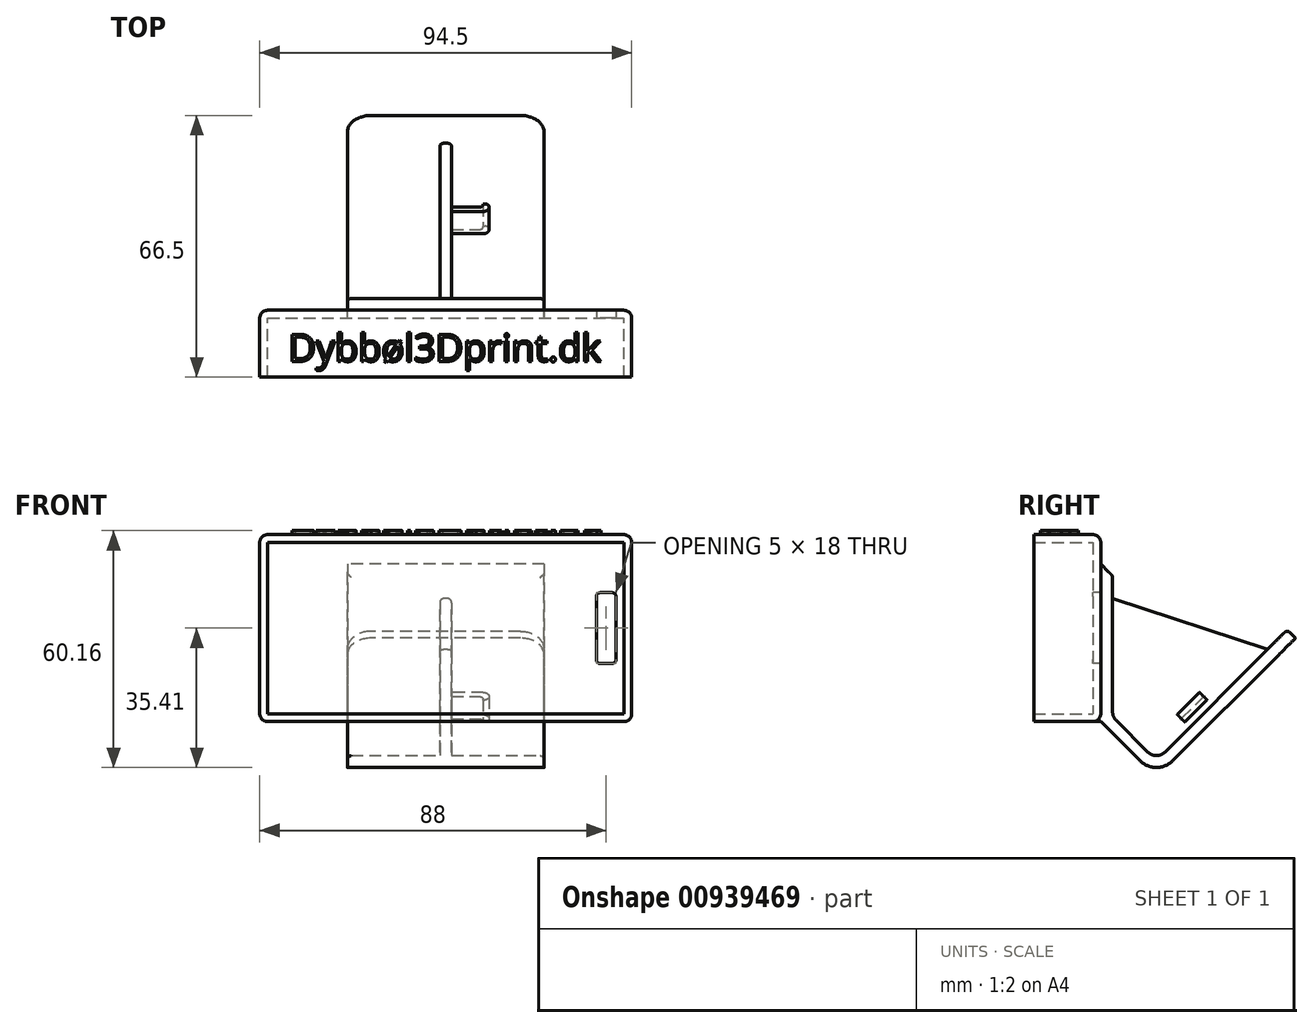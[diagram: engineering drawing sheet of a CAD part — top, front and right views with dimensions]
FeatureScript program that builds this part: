
annotation { "Feature Type Name" : "Feature", "Feature Type Description" : "" }
export const myFeature = defineFeature(function(context is Context, id is Id, definition is map)
    precondition{}
    {
        {
            var Q0;
            Q0=qCreatedBy(makeId("Front.planeOp"),FACE);
            var sketch = newSketch(context, id + "F0", { "sketchPlane" : qUnion([Q0])});
            skLineSegment(sketch, "E0.bottom", {"start": v(-47.25, 23.75) * mm, "end": v(47.25, 23.75) * mm});
            skLineSegment(sketch, "E0.top", {"start": v(-47.25, -23.75) * mm, "end": v(47.25, -23.75) * mm});
            skLineSegment(sketch, "E0.left", {"start": v(-47.25, 23.75) * mm, "end": v(-47.25, -23.75) * mm});
            skLineSegment(sketch, "E0.right", {"start": v(47.25, 23.75) * mm, "end": v(47.25, -23.75) * mm});
            skSolve(sketch);
        }
        {
            var Q0;
            Q0 = qSketchRegion(id + "F0", true);
            extrude(context, id + "F1", {"entities" : qUnion([Q0]), "depth" : 17 * mm, "offsetDistance" : 25 * mm});
        }
        {
            var Q0;
            Q0=makeQuery(id+"F1.opExtrude","CAP_FACE",FACE,{"disambiguationData":[OSD([sQuery(id+"F0.wireOp",EDGE,"E0.bottom"),sQuery(id+"F0.wireOp",EDGE,"E0.top"),sQuery(id+"F0.wireOp",EDGE,"E0.left"),sQuery(id+"F0.wireOp",EDGE,"E0.right")])],"isStart":false});
            shell(context, id + "F2", {"entities" : qUnion([Q0]), "thickness" : 2 * mm});
        }
        {
            var Q0;
            Q0=qCreatedBy(makeId("Right.planeOp"),FACE);
            var sketch = newSketch(context, id + "F3", { "sketchPlane" : qUnion([Q0])});
            skLineSegment(sketch, "E1.0", {"start": v(-17, -23.75) * mm, "end": v(0, -23.75) * mm, "construction": true});
            skLineSegment(sketch, "E2", {"start": v(0, -23.75) * mm, "end": v(14.14, -37.9) * mm});
            skLineSegment(sketch, "E3", {"start": v(14.14, -37.9) * mm, "end": v(49.5, -2.54) * mm});
            skLineSegment(sketch, "E4", {"start": v(49.5, -2.54) * mm, "end": v(47.38, -0.42) * mm});
            skLineSegment(sketch, "E5", {"start": v(47.38, -0.42) * mm, "end": v(14.14, -33.65) * mm});
            skLineSegment(sketch, "E6", {"start": v(14.14, -33.65) * mm, "end": v(3, -22.5) * mm});
            skLineSegment(sketch, "E7", {"start": v(3, -22.5) * mm, "end": v(3, 13.25) * mm});
            skLineSegment(sketch, "E8", {"start": v(0, 0) * mm, "end": v(0, -23.75) * mm});
            skLineSegment(sketch, "E9", {"start": v(0, 0) * mm, "end": v(0, 16.25) * mm});
            skLineSegment(sketch, "E10", {"start": v(0, 16.25) * mm, "end": v(3, 13.25) * mm});
            skSolve(sketch);
        }
        {
            var Q0;
            Q0 = qSketchRegion(id + "F3", true);
            extrude(context, id + "F4", {"entities" : qUnion([Q0]), "operationType" : NewBodyOperationType.ADD, "endBound" : BoundingType.SYMMETRIC, "depth" : 50 * mm, "offsetDistance" : 25 * mm});
        }
        {
            var Q0;
            Q0=qCreatedBy(makeId("Right.planeOp"),FACE);
            var sketch = newSketch(context, id + "F5", { "sketchPlane" : qUnion([Q0])});
            skLineSegment(sketch, "E11.0", {"start": v(14.14, -33.65) * mm, "end": v(3, -22.5) * mm});
            skLineSegment(sketch, "E12.0", {"start": v(3, -22.5) * mm, "end": v(3, 7.5) * mm});
            skLineSegment(sketch, "E13.0", {"start": v(42.43, -5.37) * mm, "end": v(14.14, -33.65) * mm});
            skLineSegment(sketch, "E14", {"start": v(3, 7.5) * mm, "end": v(42.43, -5.37) * mm});
            skPoint(sketch, "E15.orphan", {"position": v(47.38, -0.42) * mm});
            skPoint(sketch, "E16.orphan", {"position": v(3, 13.25) * mm});
            skSolve(sketch);
        }
        {
            var Q0;
            Q0 = qSketchRegion(id + "F5", true);
            extrude(context, id + "F6", {"entities" : qUnion([Q0]), "operationType" : NewBodyOperationType.ADD, "endBound" : BoundingType.SYMMETRIC, "depth" : 3 * mm, "offsetDistance" : 25 * mm});
        }
        {
            var Q0;
            {var subQ0=sQuery(id+"F3.wireOp",EDGE,"E6");var subQ1=sQuery(id+"F3.wireOp",EDGE,"E5");Q0=makeQuery(id+"F6.boolean.opBoolean","SPLIT",EDGE,{"disambiguationData":[TD([makeQuery(id+"F6.opExtrude","CAP_FACE",FACE,{"disambiguationData":[OSD([sQuery(id+"F5.wireOp",EDGE,"E11.0"),sQuery(id+"F5.wireOp",EDGE,"E12.0"),sQuery(id+"F5.wireOp",EDGE,"E13.0"),sQuery(id+"F5.wireOp",EDGE,"E14")])],"isStart":false})])],"derivedFrom":makeQuery(id+"F4.opExtrude","SWEPT_EDGE",EDGE,{"disambiguationData":[OSD([subQ1,subQ0])]})});}
            var Q1;
            {var subQ0=sQuery(id+"F3.wireOp",EDGE,"E7");var subQ1=sQuery(id+"F3.wireOp",EDGE,"E6");Q1=makeQuery(id+"F6.boolean.opBoolean","SPLIT",EDGE,{"disambiguationData":[TD([makeQuery(id+"F6.opExtrude","CAP_FACE",FACE,{"disambiguationData":[OSD([sQuery(id+"F5.wireOp",EDGE,"E11.0"),sQuery(id+"F5.wireOp",EDGE,"E12.0"),sQuery(id+"F5.wireOp",EDGE,"E13.0"),sQuery(id+"F5.wireOp",EDGE,"E14")])],"isStart":false})])],"derivedFrom":makeQuery(id+"F4.opExtrude","SWEPT_EDGE",EDGE,{"disambiguationData":[OSD([subQ1,subQ0])]})});}
            var Q2;
            {var subQ0=sQuery(id+"F3.wireOp",EDGE,"E6");var subQ1=sQuery(id+"F3.wireOp",EDGE,"E5");Q2=makeQuery(id+"F6.boolean.opBoolean","SPLIT",EDGE,{"disambiguationData":[TD([makeQuery(id+"F6.opExtrude","CAP_FACE",FACE,{"disambiguationData":[OSD([sQuery(id+"F5.wireOp",EDGE,"E11.0"),sQuery(id+"F5.wireOp",EDGE,"E12.0"),sQuery(id+"F5.wireOp",EDGE,"E13.0"),sQuery(id+"F5.wireOp",EDGE,"E14")])],"isStart":true})])],"derivedFrom":makeQuery(id+"F4.opExtrude","SWEPT_EDGE",EDGE,{"disambiguationData":[OSD([subQ1,subQ0])]})});}
            var Q3;
            {var subQ0=sQuery(id+"F3.wireOp",EDGE,"E7");var subQ1=sQuery(id+"F3.wireOp",EDGE,"E6");Q3=makeQuery(id+"F6.boolean.opBoolean","SPLIT",EDGE,{"disambiguationData":[TD([makeQuery(id+"F6.opExtrude","CAP_FACE",FACE,{"disambiguationData":[OSD([sQuery(id+"F5.wireOp",EDGE,"E11.0"),sQuery(id+"F5.wireOp",EDGE,"E12.0"),sQuery(id+"F5.wireOp",EDGE,"E13.0"),sQuery(id+"F5.wireOp",EDGE,"E14")])],"isStart":true})])],"derivedFrom":makeQuery(id+"F4.opExtrude","SWEPT_EDGE",EDGE,{"disambiguationData":[OSD([subQ1,subQ0])]})});}
            fillet(context, id + "F7", {"entities" : qUnion([Q0, Q1, Q2, Q3]), "tangentPropagation" : true, "radius" : 3 * mm, "defaultsChanged" : false, "vertexSettings" : [], "allowEdgeOverflow" : false});
        }
        {
            var Q0;
            Q0=makeQuery(id+"F4.opExtrude","SWEPT_EDGE",EDGE,{"disambiguationData":[OSD([sQuery(id+"F3.wireOp",EDGE,"E2"),sQuery(id+"F3.wireOp",EDGE,"E3")])]});
            var Q1;
            Q1=makeQuery(id+"F4.opExtrude","CAP_EDGE",EDGE,{"disambiguationData":[OSD([sQuery(id+"F3.wireOp",EDGE,"E4")])],"isStart":false});
            var Q2;
            Q2=makeQuery(id+"F4.opExtrude","CAP_EDGE",EDGE,{"disambiguationData":[OSD([sQuery(id+"F3.wireOp",EDGE,"E4")])],"isStart":true});
            fillet(context, id + "F8", {"entities" : qUnion([Q0, Q1, Q2]), "tangentPropagation" : true, "radius" : 6 * mm, "defaultsChanged" : false, "vertexSettings" : [], "allowEdgeOverflow" : false});
        }
        {
            var Q0;
            Q0=makeQuery(id+"F1.opExtrude","SWEPT_EDGE",EDGE,{"disambiguationData":[OSD([sQuery(id+"F0.wireOp",EDGE,"E0.bottom"),sQuery(id+"F0.wireOp",EDGE,"E0.left")])]});
            var Q1;
            Q1=makeQuery(id+"F1.opExtrude","SWEPT_EDGE",EDGE,{"disambiguationData":[OSD([sQuery(id+"F0.wireOp",EDGE,"E0.top"),sQuery(id+"F0.wireOp",EDGE,"E0.left")])]});
            var Q2;
            Q2=makeQuery(id+"F1.opExtrude","SWEPT_EDGE",EDGE,{"disambiguationData":[OSD([sQuery(id+"F0.wireOp",EDGE,"E0.top"),sQuery(id+"F0.wireOp",EDGE,"E0.right")])]});
            var Q3;
            Q3=makeQuery(id+"F1.opExtrude","SWEPT_EDGE",EDGE,{"disambiguationData":[OSD([sQuery(id+"F0.wireOp",EDGE,"E0.bottom"),sQuery(id+"F0.wireOp",EDGE,"E0.right")])]});
            fillet(context, id + "F9", {"entities" : qUnion([Q0, Q1, Q2, Q3]), "tangentPropagation" : true, "radius" : 2 * mm, "defaultsChanged" : false, "vertexSettings" : [], "allowEdgeOverflow" : false});
        }
        {
            var Q0;
            Q0=makeQuery(id+"F1.opExtrude","CAP_EDGE",EDGE,{"disambiguationData":[OSD([sQuery(id+"F0.wireOp",EDGE,"E0.bottom")])],"isStart":true});
            fillet(context, id + "F10", {"entities" : qUnion([Q0]), "tangentPropagation" : true, "radius" : 2 * mm, "defaultsChanged" : false, "vertexSettings" : [], "allowEdgeOverflow" : false});
        }
        {
            var Q0;
            Q0=makeQuery(id+"F6.opExtrude","CAP_EDGE",EDGE,{"disambiguationData":[OSD([sQuery(id+"F5.wireOp",EDGE,"E14")])],"isStart":false});
            var Q1;
            Q1=makeQuery(id+"F6.opExtrude","CAP_EDGE",EDGE,{"disambiguationData":[OSD([sQuery(id+"F5.wireOp",EDGE,"E14")])],"isStart":true});
            var Q2;
            Q2=makeQuery(id+"F4.opExtrude","CAP_EDGE",EDGE,{"disambiguationData":[OSD([sQuery(id+"F3.wireOp",EDGE,"E5")])],"isStart":false});
            var Q3;
            Q3=makeQuery(id+"F4.opExtrude","SWEPT_EDGE",EDGE,{"disambiguationData":[OSD([sQuery(id+"F3.wireOp",EDGE,"E7"),sQuery(id+"F3.wireOp",EDGE,"E10")])]});
            fillet(context, id + "F11", {"entities" : qUnion([Q0, Q1, Q2, Q3]), "tangentPropagation" : true, "radius" : 1 * mm, "defaultsChanged" : false, "vertexSettings" : [], "allowEdgeOverflow" : false});
        }
        {
            var Q0;
            Q0=makeQuery(id+"F2.opShell","OFFSET_FACE",FACE,{"disambiguationData":[OSD([sQuery(id+"F0.wireOp",EDGE,"E0.bottom"),sQuery(id+"F0.wireOp",EDGE,"E0.top"),sQuery(id+"F0.wireOp",EDGE,"E0.left"),sQuery(id+"F0.wireOp",EDGE,"E0.right")])]});
            var sketch = newSketch(context, id + "F12", { "sketchPlane" : qUnion([Q0])});
            skLineSegment(sketch, "E17.bottom", {"start": v(43.25, 9) * mm, "end": v(38.25, 9) * mm});
            skLineSegment(sketch, "E17.top", {"start": v(43.25, -9) * mm, "end": v(38.25, -9) * mm});
            skLineSegment(sketch, "E17.left", {"start": v(43.25, 9) * mm, "end": v(43.25, -9) * mm});
            skLineSegment(sketch, "E17.right", {"start": v(38.25, 9) * mm, "end": v(38.25, -9) * mm});
            skSolve(sketch);
        }
        {
            var Q0;
            Q0 = qSketchRegion(id + "F12", true);
            extrude(context, id + "F13", {"entities" : qUnion([Q0]), "operationType" : NewBodyOperationType.REMOVE, "endBound" : BoundingType.THROUGH_ALL, "oppositeDirection" : true, "depth" : 25 * mm, "offsetDistance" : 25 * mm});
        }
        {
            var Q0;
            Q0=makeQuery(id+"F13.boolean.opBoolean","COPY",EDGE,{"derivedFrom":makeQuery(id+"F13.opExtrude","SWEPT_EDGE",EDGE,{"disambiguationData":[OSD([sQuery(id+"F12.wireOp",EDGE,"E17.top"),sQuery(id+"F12.wireOp",EDGE,"E17.left")])]})});
            var Q1;
            Q1=makeQuery(id+"F13.boolean.opBoolean","COPY",EDGE,{"derivedFrom":makeQuery(id+"F13.opExtrude","SWEPT_EDGE",EDGE,{"disambiguationData":[OSD([sQuery(id+"F12.wireOp",EDGE,"E17.top"),sQuery(id+"F12.wireOp",EDGE,"E17.right")])]})});
            var Q2;
            Q2=makeQuery(id+"F13.boolean.opBoolean","COPY",EDGE,{"derivedFrom":makeQuery(id+"F13.opExtrude","SWEPT_EDGE",EDGE,{"disambiguationData":[OSD([sQuery(id+"F12.wireOp",EDGE,"E17.bottom"),sQuery(id+"F12.wireOp",EDGE,"E17.left")])]})});
            var Q3;
            Q3=makeQuery(id+"F13.boolean.opBoolean","COPY",EDGE,{"derivedFrom":makeQuery(id+"F13.opExtrude","SWEPT_EDGE",EDGE,{"disambiguationData":[OSD([sQuery(id+"F12.wireOp",EDGE,"E17.bottom"),sQuery(id+"F12.wireOp",EDGE,"E17.right")])]})});
            fillet(context, id + "F14", {"entities" : qUnion([Q0, Q1, Q2, Q3]), "tangentPropagation" : true, "radius" : 1 * mm, "defaultsChanged" : false, "vertexSettings" : [], "allowEdgeOverflow" : false});
        }
        {
            var Q0;
            Q0=makeQuery(id+"F4.opExtrude","SWEPT_FACE",FACE,{"disambiguationData":[OSD([sQuery(id+"F3.wireOp",EDGE,"E4")])]});
            cPlane(context, id + "F15", {"entities" : qUnion([Q0]), "cplaneType" : CPlaneType.OFFSET, "offset" : 35 * mm, "oppositeDirection" : true, "width" : 150 * mm, "height" : 150 * mm});
        }
        {
            var Q0;
            Q0=qCreatedBy(id+"F15.planeOp",FACE);
            var sketch = newSketch(context, id + "F16", { "sketchPlane" : qUnion([Q0])});
            skLineSegment(sketch, "E18.0", {"start": v(-1.5, -33.8) * mm, "end": v(-1.5, 2.43) * mm, "construction": true});
            skLineSegment(sketch, "E19.0.0", {"start": v(-19, -33.8) * mm, "end": v(-19, -34.8) * mm, "construction": true});
            skLineSegment(sketch, "E19.0.1", {"start": v(19, -34.8) * mm, "end": v(-19, -34.8) * mm, "construction": true});
            skLineSegment(sketch, "E19.0.2", {"start": v(19, -34.8) * mm, "end": v(19, -33.8) * mm, "construction": true});
            skLineSegment(sketch, "E19.0.3", {"start": v(19, -33.8) * mm, "end": v(-19, -33.8) * mm, "construction": true});
            skLineSegment(sketch, "E20", {"start": v(-1.5, -30.8) * mm, "end": v(-9.5, -30.8) * mm});
            skLineSegment(sketch, "E21", {"start": v(-9.5, -32) * mm, "end": v(-9.5, -30.8) * mm});
            skLineSegment(sketch, "E22", {"start": v(-9.5, -32) * mm, "end": v(-11, -32) * mm});
            skLineSegment(sketch, "E23", {"start": v(-11, -29.3) * mm, "end": v(-11, -32) * mm});
            skLineSegment(sketch, "E24", {"start": v(-11, -29.3) * mm, "end": v(-1.5, -29.3) * mm});
            skLineSegment(sketch, "E25", {"start": v(-1.5, -30.8) * mm, "end": v(-1.5, -29.3) * mm});
            skSolve(sketch);
        }
        {
            var Q0;
            Q0 = qSketchRegion(id + "F16", true);
            extrude(context, id + "F17", {"entities" : qUnion([Q0]), "operationType" : NewBodyOperationType.ADD, "depth" : 8 * mm, "offsetDistance" : 25 * mm});
        }
        {
            var Q0;
            Q0=makeQuery(id+"F17.opExtrude","SWEPT_EDGE",EDGE,{"disambiguationData":[OSD([sQuery(id+"F16.wireOp",EDGE,"E20"),sQuery(id+"F16.wireOp",EDGE,"E25")])]});
            var Q1;
            Q1=makeQuery(id+"F17.opExtrude","SWEPT_EDGE",EDGE,{"disambiguationData":[OSD([sQuery(id+"F16.wireOp",EDGE,"E24"),sQuery(id+"F16.wireOp",EDGE,"E25")])]});
            var Q2;
            Q2=makeQuery(id+"F17.opExtrude","SWEPT_EDGE",EDGE,{"disambiguationData":[OSD([sQuery(id+"F16.wireOp",EDGE,"E20"),sQuery(id+"F16.wireOp",EDGE,"E21")])]});
            var Q3;
            Q3=makeQuery(id+"F17.opExtrude","SWEPT_EDGE",EDGE,{"disambiguationData":[OSD([sQuery(id+"F16.wireOp",EDGE,"E22"),sQuery(id+"F16.wireOp",EDGE,"E23")])]});
            fillet(context, id + "F18", {"entities" : qUnion([Q0, Q1, Q2, Q3]), "tangentPropagation" : true, "radius" : 1 * mm, "defaultsChanged" : false, "vertexSettings" : [], "allowEdgeOverflow" : false});
        }
        {
            var Q0;
            Q0=makeQuery(id+"F17.opExtrude","SWEPT_EDGE",EDGE,{"disambiguationData":[OSD([sQuery(id+"F16.wireOp",EDGE,"E23"),sQuery(id+"F16.wireOp",EDGE,"E24")])]});
            fillet(context, id + "F19", {"entities" : qUnion([Q0]), "tangentPropagation" : true, "radius" : 1.5 * mm, "defaultsChanged" : true, "vertexSettings" : [], "allowEdgeOverflow" : false});
        }
        {
            var Q0;
            Q0=makeQuery(id+"F1.opExtrude","SWEPT_FACE",FACE,{"disambiguationData":[OSD([sQuery(id+"F0.wireOp",EDGE,"E0.bottom")])]});
            var sketch = newSketch(context, id + "F20", { "sketchPlane" : qUnion([Q0])});
            skText(sketch, "E26", { "text": "Dybbøl3Dprint.dk", "fontName": "OpenSans-Regular.ttf"});
            const initialGuessF20  = {"E26": [-0.04, -0.013, 1, 0, 0.00693]};
            skSetInitialGuess(sketch, initialGuessF20);
            skSolve(sketch);
        }
        {
            var Q0;
            Q0 = qSketchRegion(id + "F20", true);
            extrude(context, id + "F21", {"entities" : qUnion([Q0]), "operationType" : NewBodyOperationType.ADD, "depth" : 1 * mm, "offsetDistance" : 25 * mm});
        }
    });
